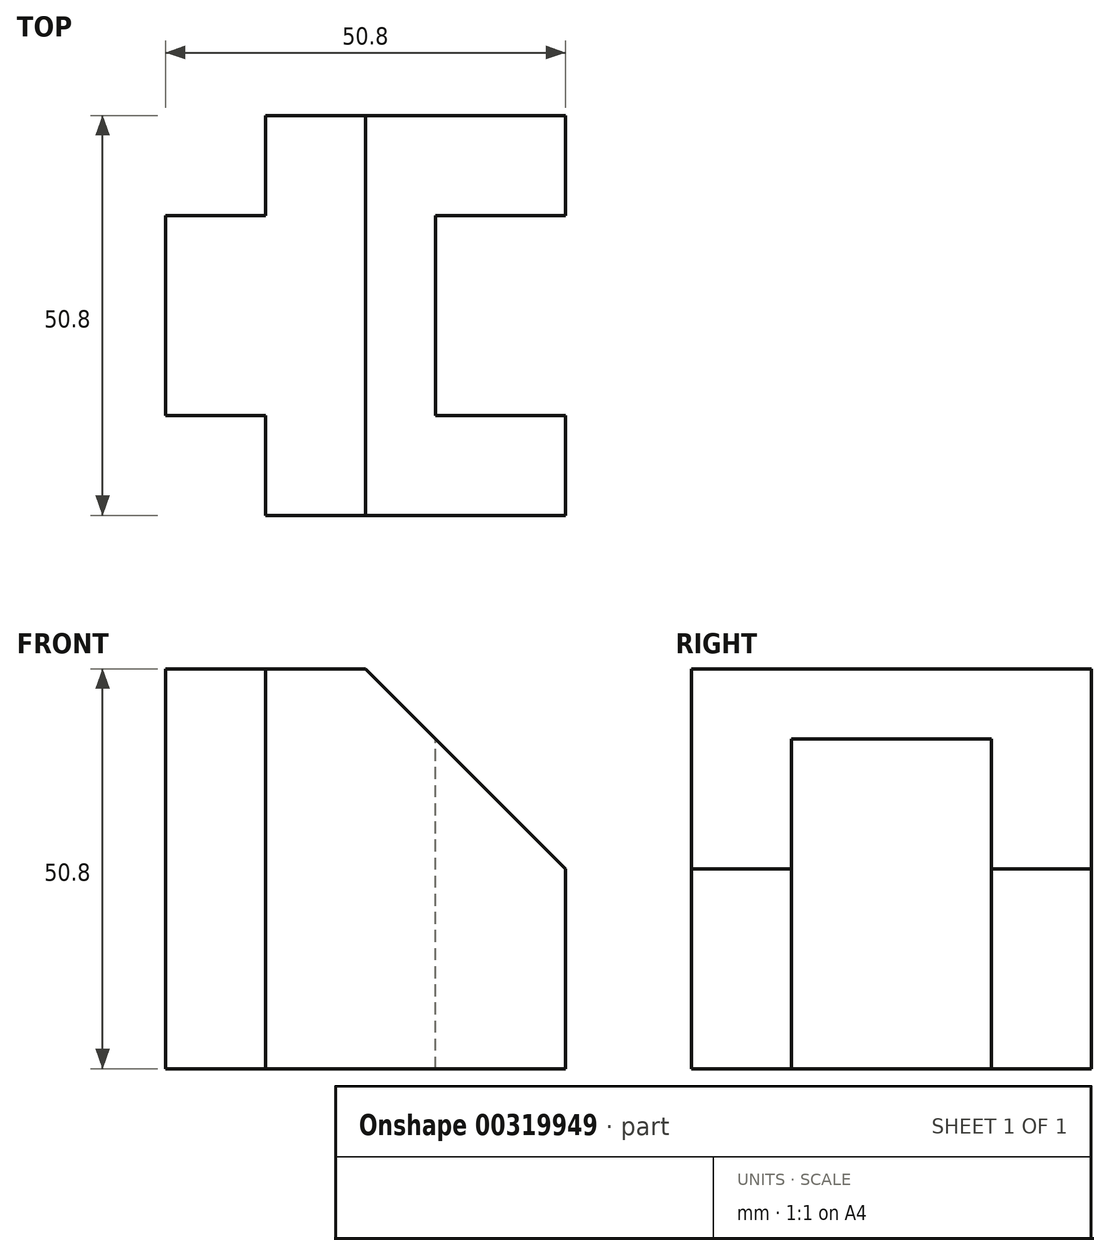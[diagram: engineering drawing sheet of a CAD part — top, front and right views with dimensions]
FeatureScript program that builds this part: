
annotation { "Feature Type Name" : "Feature", "Feature Type Description" : "" }
export const myFeature = defineFeature(function(context is Context, id is Id, definition is map)
    precondition{}
    {
        {
            var Q0;
            Q0=qCreatedBy(makeId("Front.planeOp"),FACE);
            var sketch = newSketch(context, id + "F0", { "sketchPlane" : qUnion([Q0])});
            skLineSegment(sketch, "E0", {"start": v(0, 0) * mm, "end": v(0, 50.8) * mm});
            skLineSegment(sketch, "E1", {"start": v(0, 50.8) * mm, "end": v(25.4, 50.8) * mm});
            skLineSegment(sketch, "E2", {"start": v(25.4, 0) * mm, "end": v(0, 0) * mm});
            skLineSegment(sketch, "E3", {"start": v(25.4, 50.8) * mm, "end": v(50.8, 25.4) * mm});
            skLineSegment(sketch, "E4", {"start": v(50.8, 25.4) * mm, "end": v(50.8, 0) * mm});
            skLineSegment(sketch, "E5", {"start": v(50.8, 0) * mm, "end": v(25.4, 0) * mm});
            skLineSegment(sketch, "E6", {"start": v(12.7, 50.8) * mm, "end": v(12.7, 0) * mm});
            skSolve(sketch);
        }
        {
            var Q0;
            Q0=makeQuery(id+"F0.imprint","IMPRINT",FACE,{"disambiguationData":[TD([[makeQuery(id+"F0.imprint","IMPRINT",EDGE,{"derivedFrom":sQuery(id+"F0.wireOp",EDGE,"Ug2j92ih-hoAd-Llly-EZe6-B2dHUB4ykU0z")}),1.0]])]});
            var Q1;
            Q1=makeQuery(id+"F0.imprint","IMPRINT",FACE,{"disambiguationData":[TD([[makeQuery(id+"F0.imprint","IMPRINT",EDGE,{"derivedFrom":sQuery(id+"F0.wireOp",EDGE,"E0")}),-1.0]])]});
            var Q2;
            {var subQ0=sQuery(id+"F0.wireOp",EDGE,"E3");Q2=makeQuery(id+"F0.imprint","IMPRINT",FACE,{"disambiguationData":[TD([[makeQuery(id+"F0.imprint","IMPRINT",EDGE,{"derivedFrom":subQ0}),-1.0]])]});}
            extrude(context, id + "F1", {"entities" : qUnion([Q0, Q1, Q2]), "depth" : 50.8 * mm, "symmetric" : true});
        }
        {
            var Q0;
            Q0=makeQuery(id+"F1.opExtrude","SWEPT_FACE",FACE,{"disambiguationData":[OSD([sQuery(id+"F0.wireOp",EDGE,"E1")])]});
            var sketch = newSketch(context, id + "F2", { "sketchPlane" : qUnion([Q0])});
            skLineSegment(sketch, "E7", {"start": v(12.7, 25.4) * mm, "end": v(12.7, 12.7) * mm});
            skLineSegment(sketch, "E8", {"start": v(12.7, 12.7) * mm, "end": v(0, 12.7) * mm});
            skLineSegment(sketch, "E9", {"start": v(12.7, -25.4) * mm, "end": v(12.7, -12.7) * mm});
            skLineSegment(sketch, "E10", {"start": v(12.7, -12.7) * mm, "end": v(0, -12.7) * mm});
            skLineSegment(sketch, "E11.0", {"start": v(50.8, -25.4) * mm, "end": v(50.8, 25.4) * mm});
            skLineSegment(sketch, "E12.0", {"start": v(25.4, 25.4) * mm, "end": v(50.8, 25.4) * mm});
            skLineSegment(sketch, "E13.0", {"start": v(25.4, -25.4) * mm, "end": v(25.4, 25.4) * mm});
            skLineSegment(sketch, "E14.0", {"start": v(25.4, -25.4) * mm, "end": v(50.8, -25.4) * mm});
            skLineSegment(sketch, "E15", {"start": v(50.8, 12.7) * mm, "end": v(34.3, 12.7) * mm});
            skLineSegment(sketch, "E16", {"start": v(34.3, 12.7) * mm, "end": v(34.3, -12.7) * mm});
            skLineSegment(sketch, "E17", {"start": v(34.3, -12.7) * mm, "end": v(50.8, -12.7) * mm});
            skSolve(sketch);
        }
        {
            var Q0;
            {var subQ0=sQuery(id+"F2.wireOp",EDGE,"E9");Q0=makeQuery(id+"F2.imprint","IMPRINT",FACE,{"disambiguationData":[TD([[makeQuery(id+"F2.imprint","IMPRINT",EDGE,{"derivedFrom":subQ0}),1.0]])]});}
            var Q1;
            {var subQ0=sQuery(id+"F2.wireOp",EDGE,"E7");Q1=makeQuery(id+"F2.imprint","IMPRINT",FACE,{"disambiguationData":[TD([[makeQuery(id+"F2.imprint","IMPRINT",EDGE,{"derivedFrom":subQ0}),-1.0]])]});}
            var Q2;
            {var subQ0=sQuery(id+"F2.wireOp",EDGE,"E15");Q2=makeQuery(id+"F2.imprint","IMPRINT",FACE,{"disambiguationData":[TD([[makeQuery(id+"F2.imprint","IMPRINT",EDGE,{"derivedFrom":subQ0}),1.0]])]});}
            extrude(context, id + "F3", {"entities" : qUnion([Q0, Q1, Q2]), "operationType" : NewBodyOperationType.REMOVE, "endBound" : BoundingType.THROUGH_ALL, "oppositeDirection" : true, "depth" : 25.4 * mm});
        }
    });
